# Revit family: Faucet-Wall_Mount-Bath_Spout-KOHLER-PURIST-K-14426T
name_source: partatom
category: Plumbing Fixtures
revit_build: Autodesk Revit 2017 (Build: 20160225_1515(x64)
units: mm (PartAtom-declared; Revit-internal decimal feet)

## family parameters
Cut with Voids When Loaded = No
Host = Face
OmniClass Number = 23.31.11.00
OmniClass Title = Faucets
Part Type = Normal
Room Calculation Point = No
Round Connector Dimension = Use Diameter
Shared = No

## types (5) — shared parameters
ADA Compliant = No
CW Connection = Yes
Cold Water Inlet = Cold Water Inlet
Date Modified = 06/10/2020
Default Elevation = 36"
Description = Outlet of Bathtub
Drain Included = No
Flow Rate = 0 GPM
HW Connection = Yes
Height = 4"
Hot Water Inlet = Tempered Water Inlet
Length = 8 1/16"
Manufacturer = KOHLER Co.
Master Format 2014 = 22 41 39
Master Format 2014 Name = Residential Faucets, Supplies, and Trim
Material = Premium Metal Construction
Pressure = 0.00 psi
Product Documentation Link = http://files.kohler.com.cn
Product Name = PURIST
Product Page URL = http://www.kohler.com.cn
Spout Reach = 8 1/16"
URL = http://www.kohler.com.cn
Vent Connection = No
Waste Connection = No
Waste Water Outlet = Waste Water Outlet
WaterSense Certified = No
Width = 4"

## per-type parameters (varying)
| type | Assembly Code | Finish | Model | Type |
| CP-Polished Chrome | D2010 | Kohler-Metal-CP-Polished_Chrome | K-14426T-CP | 1 |
| RGD-Rose Gold | D2010700 | Kohler-Metal-BGD-Romankin | K-14426T-RGD | 2 |
| BN-Roman Silver | D2010700 | Kohler-Metal-BN-Roman_Silver | K-14426T-BN | 3 |
| SN-Champagne Gold | D2010700 | Kohler-Metal-SN-Champagne_Gold | K-14426T-SN | 4 |
| PGD-Eternal Gold | D2010700 | Kohler-Metal-PGD-Eternal_Gold | K-14426T-PGD | 5 |

## geometry (parser evidence)
native form markers: Sweep x4
no freeform markers — native parametric forms only
